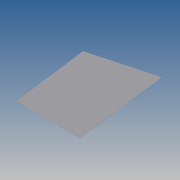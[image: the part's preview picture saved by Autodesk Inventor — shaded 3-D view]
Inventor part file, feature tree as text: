
AUTODESK INVENTOR PART (.ipt)
format: ipt  version: 2014 SP1 (Build 180222100, 222)  size: 71,680 bytes
history: native  units: in
note: dims shown in document units (in); Inventor stores cm internally (conversion verified against a paired STEP export)
features: extrude x1, sketch x1
ambient origin geometry x8: Origin, YZ Plane, XZ Plane, XY Plane, X Axis, Y Axis, Z Axis, Center Point
bodies: Solid1 (feature_tree)
feature tree (2):
  extrude  "Extrusion1"  Depth=0.0394in
  sketch  "Sketch1"  dims[d2=165.0deg d5=207.4803in d6=1.1853in d7=1.9685in d8=1.9685in d9=0.0394in d10=0.0in]
